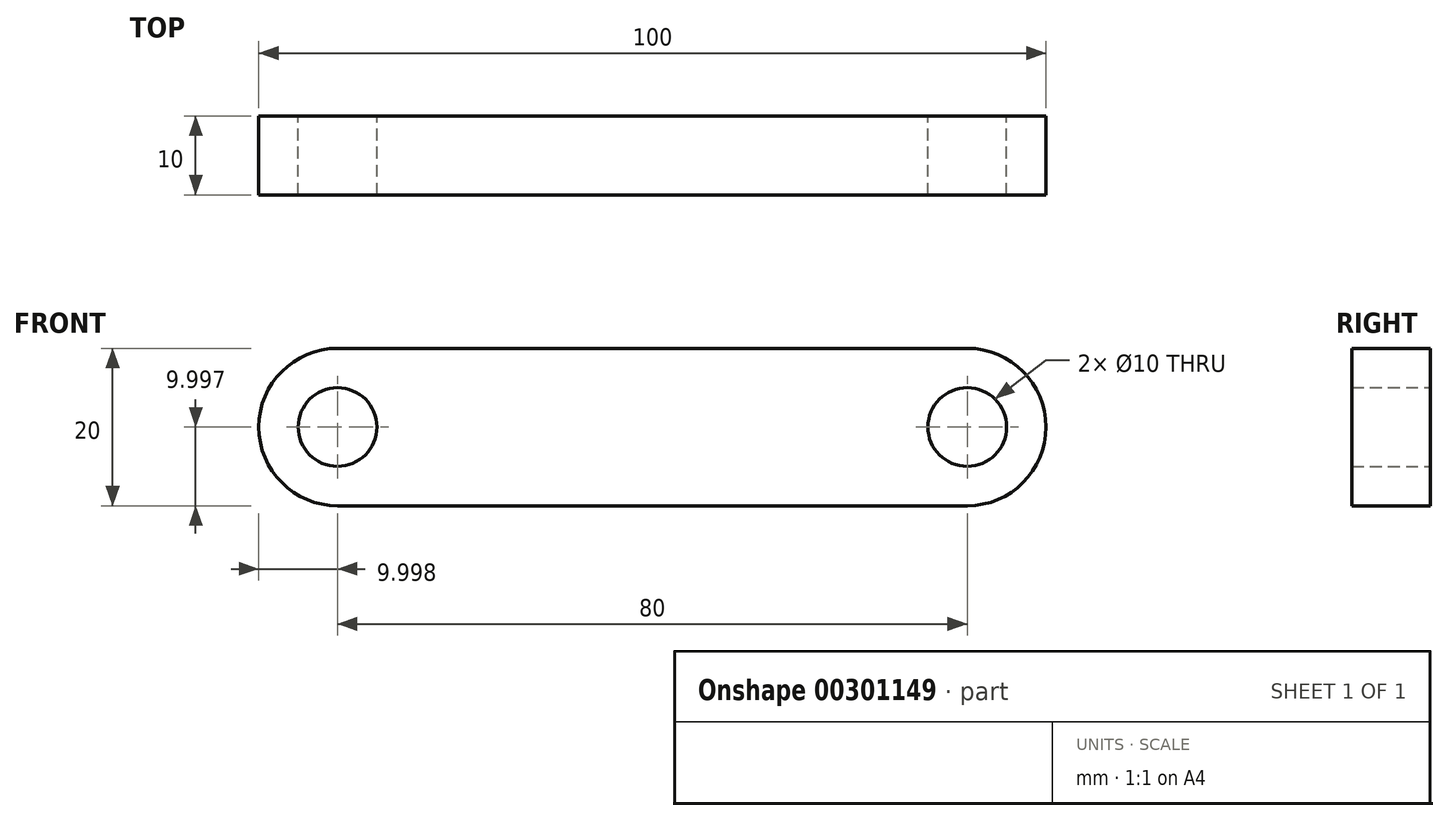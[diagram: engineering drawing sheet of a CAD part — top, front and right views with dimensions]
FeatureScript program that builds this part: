
annotation { "Feature Type Name" : "Feature", "Feature Type Description" : "" }
export const myFeature = defineFeature(function(context is Context, id is Id, definition is map)
    precondition{}
    {
        {
            var Q0;
            Q0=qCreatedBy(makeId("Front.planeOp"),FACE);
            var sketch = newSketch(context, id + "F0", { "sketchPlane" : qUnion([Q0])});
            skLineSegment(sketch, "E0", {"start": v(-29.12, 0.06) * mm, "end": v(50.88, 0.06) * mm});
            skLineSegment(sketch, "E1", {"start": v(-29.12, -19.94) * mm, "end": v(50.88, -19.94) * mm});
            skArc(sketch, "E2", {"start": v(50.88, -19.94) * mm, "mid": v(60.88, -9.94) * mm, "end": v(50.88, 0.06) * mm});
            skArc(sketch, "E3", {"start": v(-29.12, 0.06) * mm, "mid": v(-39.12, -9.94) * mm, "end": v(-29.12, -19.94) * mm});
            skCircle(sketch, "E4", {"center": v(-29.12, -9.94) * mm, "radius": 5 * mm});
            skCircle(sketch, "E5", {"center": v(50.88, -9.94) * mm, "radius": 5 * mm});
            skSolve(sketch);
        }
        {
            var Q0;
            Q0 = qSketchRegion(id + "F0", true);
            extrude(context, id + "F1", {"entities" : qUnion([Q0]), "depth" : 10 * mm});
        }
    });
